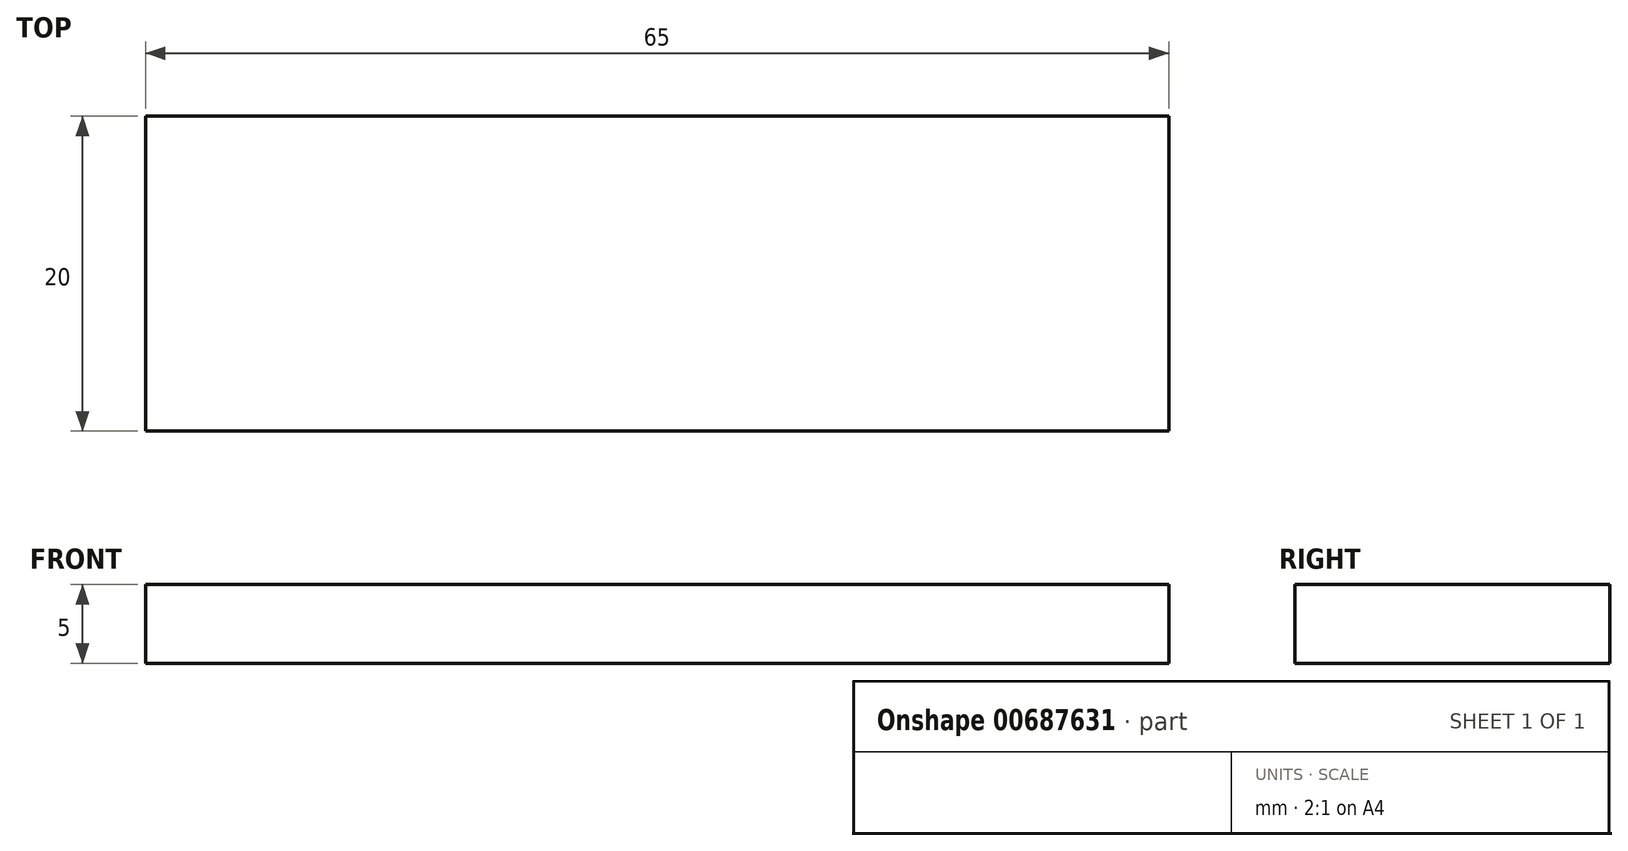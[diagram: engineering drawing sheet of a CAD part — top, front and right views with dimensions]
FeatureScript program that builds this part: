
annotation { "Feature Type Name" : "Feature", "Feature Type Description" : "" }
export const myFeature = defineFeature(function(context is Context, id is Id, definition is map)
    precondition{}
    {
        {
            var Q0;
            Q0=qCreatedBy(makeId("Top.planeOp"),FACE);
            var sketch = newSketch(context, id + "F0", { "sketchPlane" : qUnion([Q0])});
            skLineSegment(sketch, "E0.bottom", {"start": v(-10.16, 23.42) * mm, "end": v(54.84, 23.42) * mm});
            skLineSegment(sketch, "E0.top", {"start": v(-10.16, 3.42) * mm, "end": v(54.84, 3.42) * mm});
            skLineSegment(sketch, "E0.left", {"start": v(-10.16, 23.42) * mm, "end": v(-10.16, 3.42) * mm});
            skLineSegment(sketch, "E0.right", {"start": v(54.84, 23.42) * mm, "end": v(54.84, 3.42) * mm});
            skSolve(sketch);
        }
        {
            var Q0;
            Q0 = qSketchRegion(id + "F0", true);
            extrude(context, id + "F1", {"entities" : qUnion([Q0]), "depth" : 5 * mm, "offsetDistance" : 25 * mm});
        }
    });
